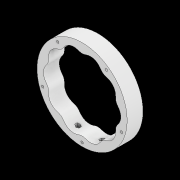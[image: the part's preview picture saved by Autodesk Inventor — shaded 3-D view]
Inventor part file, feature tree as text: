
AUTODESK INVENTOR PART (.ipt)
format: ipt  version: 2022.2 (Build 262287010, 287A)  size: 359,936 bytes
history: native  units: mm
features: sketch x11, extrude x10, other x3, pattern_circular x3, plane x1, hole x1, fillet x1
ambient origin geometry x8: Origin, YZ Plane, XZ Plane, XY Plane, X Axis, Y Axis, Z Axis, Center Point
bodies: Solid3 (feature_tree)
feature tree (30):
  other  "CrossSection1"
  sketch  "Sketch3"  dims[d59=66.75mm d61=0.0mm d62=3600.0mm]
  sketch  "Sketch1"  dims[d4=150.0mm d19=12.0mm]
  plane  "Work Plane1"
  sketch  "Sketch9"  dims[d91=23.65mm d93=60.0mm]
  extrude  "Extrusion7"  Depth=12.0mm
  sketch  "Sketch10"  dims[d94=30.0mm d95=200.000423mm]
  extrude  "Extrusion10"  Depth=3600.0mm TaperAngle=0.0deg
  pattern_circular  "Circular Pattern4"  Count=6  [1 undecoded]
  extrude  "Extrusion8"  Depth=200.000423mm
  extrude  "Extrusion9"  Depth=26.0mm TaperAngle=0.0deg
  pattern_circular  "Circular Pattern3"  [2 undecoded]
  extrude  "Extrusion3"  Depth=2.0mm TaperAngle=0.0deg
  hole  "Hole3"  [1 undecoded]
  pattern_circular  "Circular Pattern5"  [2 undecoded]
  sketch  "Sketch13"  dims[d102=29.0mm d103=0.0mm d104=2.0mm d105=0.0mm d106=3600.0mm d111=100.0mm d112=69.0mm d113=2.5mm d114=0.0mm d115=3.0mm d116=0.0mm d117=0.0mm d118=5.5mm d119=2.5mm d120=0.0mm d121=50.0mm d122=360.0deg d124=2.5mm d125=0.0mm d126=50.0mm d127=360.0deg d129=22.5mm d130=2.5mm d131=0.0mm d132=138.0mm d133=4.0mm d134=6.0mm d135=4.0mm d136=2.0mm d137=90.0deg d138=4.0mm d139=0.0mm d140=50.0mm d141=360.0deg d143=0.5mm d144=2.0mm d145=0.0mm d146=20.0mm d147=3.1416mm d148=3.141586mm d149=7.0mm d150=7.0mm d151=65.564mm d152=0.0mm d153=4.0mm d154=4.0mm d155=0.0mm d156=0.0mm d157=82.0mm d158=30.0mm d159=4.0mm d160=4.0mm]
  extrude  "Extrusion12"  Depth=2.0mm TaperAngle=0.0deg
  extrude  "Extrusion13"  Depth=2.0mm
  sketch  "Sketch4"  dims[d66=12.0mm]
  sketch  "Sketch5"  dims[d67=63.483mm]
  extrude  "Extrusion4"  TaperAngle=0.0deg  [1 undecoded]
  sketch  "Sketch7"  dims[d68=138.0mm]
  extrude  "Extrusion6"  Depth=2.0mm
  fillet  "Fillet1"  Radius=2.5mm
  extrude  "Extrusion11"  Depth=2.0mm TaperAngle=360.0deg
  other  "2D Equation Curve10"
  sketch  "Sketch8"  dims[d69=26.3mm d70=0.0mm]
  other  "2D Equation Curve11"
  sketch  "Sketch11"  dims[d96=23.65mm d97=26.0mm d98=0.0mm]
  sketch  "Sketch12"  dims[d99=156.0mm]
note: 7 required parameter values undecoded (feature->parameter linkage not recoverable at this tier; creation-order binding heuristic only, values carry confidence <= 0.55)
